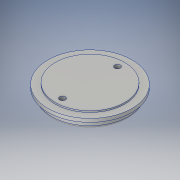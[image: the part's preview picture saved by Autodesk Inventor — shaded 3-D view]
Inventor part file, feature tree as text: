
AUTODESK INVENTOR PART (.ipt)
format: ipt  version: 2017 (Build 210142000, 142)  size: 146,432 bytes
history: native  units: in
note: dims shown in document units (in); Inventor stores cm internally (conversion verified against a paired STEP export)
features: sketch x2, revolve x1, hole x1, fillet x1
ambient origin geometry x8: Origin, YZ Plane, XZ Plane, XY Plane, X Axis, Y Axis, Z Axis, Center Point
bodies: Solid1 (feature_tree)
feature tree (5):
  revolve  "Revolution1"  [1 undecoded]
  hole  "Hole1"  [1 undecoded]
  fillet  "Fillet1"  Radius=1.4975in
  sketch  "Sketch1"  dims[d1=0.5in d3=0.147in d5=0.195in d8=0.691in d9=1.668in]
  sketch  "Sketch2"  dims[d10=1.814in d11=0.062in d12=1.4975in d13=90.0deg d14=2.376in d15=0.25in d16=0.75in d17=0.375in d18=0.25in d19=0.5635in d20=0.3in d21=0.0in d22=0.125in]
note: 2 required parameter values undecoded (feature->parameter linkage not recoverable at this tier; creation-order binding heuristic only, values carry confidence <= 0.55)